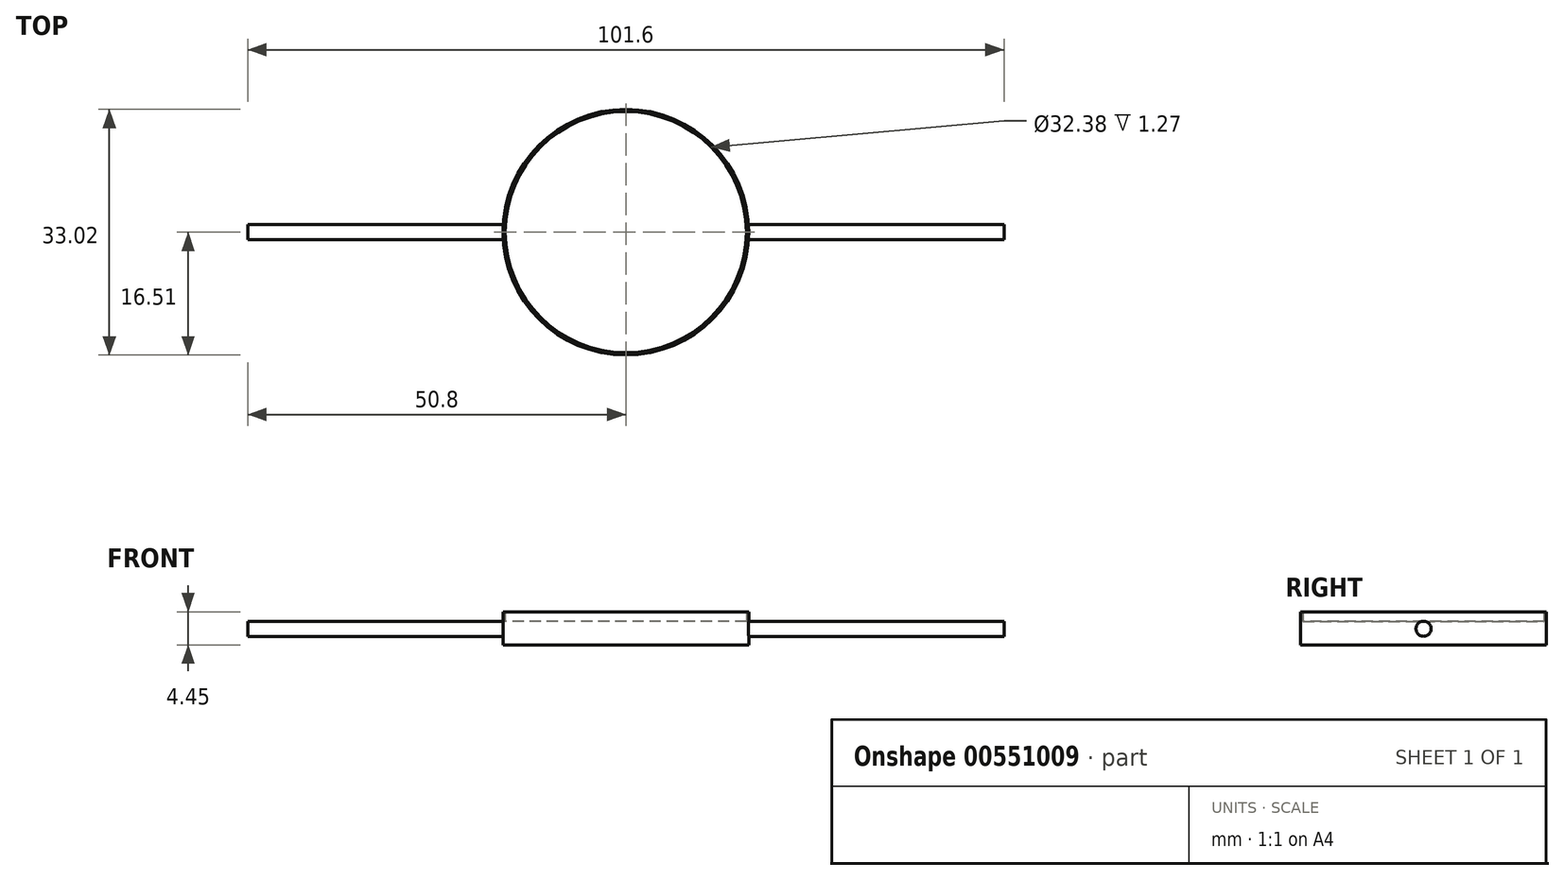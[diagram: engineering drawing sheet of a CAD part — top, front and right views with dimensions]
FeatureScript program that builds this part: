
annotation { "Feature Type Name" : "Feature", "Feature Type Description" : "" }
export const myFeature = defineFeature(function(context is Context, id is Id, definition is map)
    precondition{}
    {
        {
            var Q0;
            Q0=qCreatedBy(makeId("Top.planeOp"),FACE);
            var sketch = newSketch(context, id + "F0", { "sketchPlane" : qUnion([Q0])});
            skCircle(sketch, "E0", {"center": v(0, 0) * mm, "radius": 16.51 * mm});
            skSolve(sketch);
        }
        {
            var Q0;
            Q0 = qSketchRegion(id + "F0", true);
            extrude(context, id + "F1", {"entities" : qUnion([Q0]), "depth" : 3.17 * mm, "offsetDistance" : 25.4 * mm});
        }
        {
            var Q0;
            Q0=makeQuery(id+"F1.opExtrude","CAP_FACE",FACE,{"disambiguationData":[OSD([sQuery(id+"F0.wireOp",EDGE,"E0")])],"isStart":false});
            var sketch = newSketch(context, id + "F2", { "sketchPlane" : qUnion([Q0])});
            skCircle(sketch, "E1", {"center": v(0, 0) * mm, "radius": 16.2 * mm});
            skCircle(sketch, "E2", {"center": v(0, 0) * mm, "radius": 16.51 * mm});
            skSolve(sketch);
        }
        {
            var Q0;
            Q0 = qSketchRegion(id + "F2", true);
            extrude(context, id + "F3", {"entities" : qUnion([Q0]), "operationType" : NewBodyOperationType.ADD, "depth" : 1.27 * mm, "offsetDistance" : 25.4 * mm});
        }
        {
            var Q0;
            Q0=qCreatedBy(makeId("Right.planeOp"),FACE);
            var sketch = newSketch(context, id + "F4", { "sketchPlane" : qUnion([Q0])});
            skCircle(sketch, "E3", {"center": v(0, 2.16) * mm, "radius": 1.02 * mm});
            skSolve(sketch);
        }
        {
            var Q0;
            Q0 = qSketchRegion(id + "F4", true);
            extrude(context, id + "F5", {"entities" : qUnion([Q0]), "operationType" : NewBodyOperationType.ADD, "depth" : 50.8 * mm, "offsetDistance" : 25.4 * mm, "hasSecondDirection" : true, "secondDirectionOppositeDirection" : true, "secondDirectionDepth" : 50.8 * mm});
        }
    });
